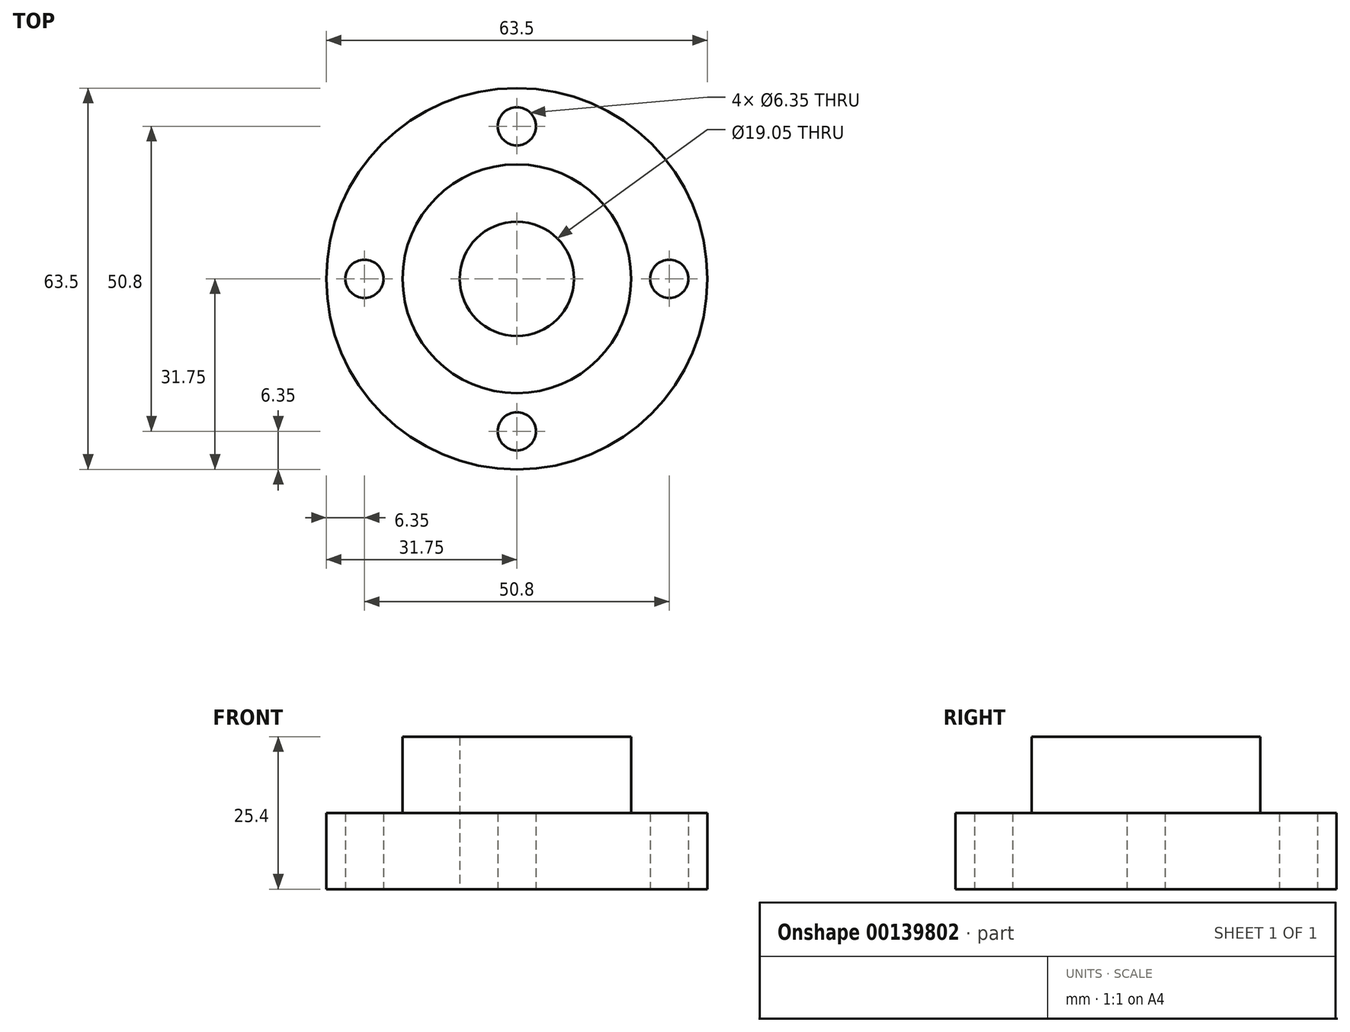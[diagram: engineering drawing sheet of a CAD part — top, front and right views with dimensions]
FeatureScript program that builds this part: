
annotation { "Feature Type Name" : "Feature", "Feature Type Description" : "" }
export const myFeature = defineFeature(function(context is Context, id is Id, definition is map)
    precondition{}
    {
        {
            var Q0;
            Q0=qCreatedBy(makeId("Top.planeOp"),FACE);
            var sketch = newSketch(context, id + "F0", { "sketchPlane" : qUnion([Q0])});
            skCircle(sketch, "E0", {"center": v(0, 0) * mm, "radius": 19.05 * mm});
            skCircle(sketch, "E1", {"center": v(0, 0) * mm, "radius": 31.75 * mm});
            skPoint(sketch, "E2", {"position": v(0, 25.4) * mm});
            skCircle(sketch, "E3", {"center": v(0, 0) * mm, "radius": 25.4 * mm});
            skPoint(sketch, "E4", {"position": v(-25.4, 0) * mm});
            skPoint(sketch, "E5", {"position": v(25.4, 0) * mm});
            skPoint(sketch, "E6", {"position": v(0, -25.4) * mm});
            skSolve(sketch);
        }
        {
            var Q0;
            Q0=makeQuery(id+"F0.imprint","IMPRINT",FACE,{"disambiguationData":[TD([[makeQuery(id+"F0.imprint","IMPRINT",EDGE,{"derivedFrom":sQuery(id+"F0.wireOp",EDGE,"E0")}),1.0]])]});
            extrude(context, id + "F1", {"entities" : qUnion([Q0]), "depth" : 25.4 * mm});
        }
        {
            var Q0;
            Q0=makeQuery(id+"F0.imprint","IMPRINT",FACE,{"disambiguationData":[TD([[makeQuery(id+"F0.imprint","IMPRINT",EDGE,{"derivedFrom":sQuery(id+"F0.wireOp",EDGE,"E0")}),-1.0]])]});
            extrude(context, id + "F2", {"entities" : qUnion([Q0]), "operationType" : NewBodyOperationType.ADD, "depth" : 12.7 * mm});
        }
        {
            var Q0;
            Q0=makeQuery(id+"F0.imprint","IMPRINT",FACE,{"disambiguationData":[TD([[makeQuery(id+"F0.imprint","IMPRINT",EDGE,{"derivedFrom":sQuery(id+"F0.wireOp",EDGE,"E1")}),1.0]])]});
            var Q1;
            Q1=sQuery(id+"F0.wireOp",EDGE,"E1");
            extrude(context, id + "F3", {"entities" : qUnion([Q0]), "operationType" : NewBodyOperationType.ADD, "surfaceEntities" : qUnion([Q1]), "depth" : 12.7 * mm});
        }
        {
            var Q0;
            Q0=sQuery(id+"F0.wireOp",VERTEX,"E2");
            var Q1;
            Q1=makeQuery(id+"F1.opExtrude","SWEPT_BODY",BODY,{"disambiguationData":[OSD([sQuery(id+"F0.wireOp",EDGE,"E0")])]});
            hole(context, id + "F4", {"style" : HoleStyle.SIMPLE, "endStyle" : HoleEndStyle.THROUGH, "oppositeDirection" : true, "holeDiameter" : 6.35 * mm, "locations" : qUnion([Q0]), "scope" : qUnion([Q1]), "isTappedThrough" : true});
        }
        {
            var Q0;
            Q0=sQuery(id+"F0.wireOp",VERTEX,"E4");
            var Q1;
            Q1=sQuery(id+"F0.wireOp",VERTEX,"E5");
            var Q2;
            Q2=sQuery(id+"F0.wireOp",VERTEX,"E6");
            var Q3;
            Q3=makeQuery(id+"F1.opExtrude","SWEPT_BODY",BODY,{"disambiguationData":[OSD([sQuery(id+"F0.wireOp",EDGE,"E0")])]});
            hole(context, id + "F5", {"style" : HoleStyle.SIMPLE, "endStyle" : HoleEndStyle.THROUGH, "oppositeDirection" : true, "holeDiameter" : 6.35 * mm, "locations" : qUnion([Q0, Q1, Q2]), "scope" : qUnion([Q3]), "isTappedThrough" : true});
        }
        {
            var Q0;
            Q0=sQuery(id+"F0.wireOp",VERTEX,"E0.center");
            var Q1;
            Q1=makeQuery(id+"F1.opExtrude","SWEPT_BODY",BODY,{"disambiguationData":[OSD([sQuery(id+"F0.wireOp",EDGE,"E0")])]});
            hole(context, id + "F6", {"style" : HoleStyle.SIMPLE, "endStyle" : HoleEndStyle.THROUGH, "oppositeDirection" : true, "holeDiameter" : 19.05 * mm, "locations" : qUnion([Q0]), "scope" : qUnion([Q1]), "isTappedThrough" : true});
        }
    });
